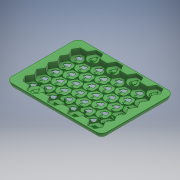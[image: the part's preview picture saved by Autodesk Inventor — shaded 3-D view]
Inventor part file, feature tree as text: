
AUTODESK INVENTOR PART (.ipt)
format: ipt  version: 2018 (Build 220112000, 112)  size: 8,218,624 bytes
history: native  units: mm
features: projected_geometry x23, extrude x22, sketch x19, pattern_linear x5, mirror x2, sweep x1, plane x1
ambient origin geometry x8: Origin, YZ Plane, XZ Plane, XY Plane, X Axis, Y Axis, Z Axis, Center Point
bodies: Solid1 (feature_tree)
feature tree (73):
  sketch  "Sketch1"  dims[d0=191.364mm d1=265.006mm]
  extrude  "Extrusion1"  Depth=265.006mm
  sketch  "Sketch2"  dims[d2=35.5mm d21=227.899911mm]
  extrude  "Extrusion3"  Depth=35.5mm
  sweep  "Sweep3"
  sketch  "Sketch6"  dims[d24=50.0mm d26=36.5mm d27=10.0mm d29=10.0mm]
  extrude  "Extrusion4"  Depth=10.0mm
  extrude  "Extrusion6"  Depth=10.0mm
  sketch  "Sketch7"  dims[d31=20.0mm d33=36.5mm d34=10.0mm d36=10.0mm]
  extrude  "Extrusion5"  Depth=10.0mm
  pattern_linear  "Rectangular Pattern1"  Count1=2 Spacing1=36.5mm
  extrude  "Extrusion7"  Depth=10.0mm
  extrude  "Extrusion8"  Depth=1.0mm
  extrude  "Extrusion9"  TaperAngle=0.0deg  [1 undecoded]
  sketch  "Sketch14"  dims[d45=16.65mm d46=0.0mm]
  extrude  "Extrusion12"  Depth=10.0mm TaperAngle=0.0deg
  extrude  "Extrusion13"  Depth=40.0mm
  extrude  "Extrusion15"  Depth=5.0mm TaperAngle=0.0deg
  extrude  "Extrusion16"  Depth=182.5mm
  extrude  "Extrusion17"  Depth=5.0mm TaperAngle=0.0deg
  extrude  "Extrusion27"  Depth=1.0mm TaperAngle=0.0deg
  extrude  "Extrusion18"  Depth=36.5mm
  extrude  "Extrusion19"  Depth=10.0mm
  extrude  "Extrusion20"  Depth=5.0mm TaperAngle=0.0deg
  plane  "Work Plane1"
  mirror  "Mirror1"
  pattern_linear  "Rectangular Pattern3"  Spacing1=0.5mm  [1 undecoded]
  pattern_linear  "Rectangular Pattern4"  Spacing1=11.65mm  [1 undecoded]
  extrude  "Extrusion21"  TaperAngle=0.0deg  [1 undecoded]
  extrude  "Extrusion22"  Depth=16.0mm
  extrude  "Extrusion23"  Depth=10.0mm
  pattern_linear  "Rectangular Pattern5"  Count1=8 Spacing1=31.609927mm
  pattern_linear  "Rectangular Pattern6"  Spacing1=11.65mm  [1 undecoded]
  mirror  "Mirror2"
  extrude  "Extrusion24"  TaperAngle=0.0deg  [1 undecoded]
  extrude  "Extrusion28"  Depth=16.0mm
  projected_geometry  "Projected Loop1"
  sketch  "Sketch5"  dims[d22=301.559911mm d23=18.288mm]
  projected_geometry  "Projected Loop3"
  projected_geometry  "Projected Loop4"
  sketch  "Sketch11"  dims[d38=40.0mm d40=63.219854mm d41=10.0mm d43=10.0mm]
  projected_geometry  "Projected Loop10"
  projected_geometry  "Projected Loop11"
  projected_geometry  "Projected Loop18"
  projected_geometry  "Projected Loop19"
  projected_geometry  "Projected Loop20"
  sketch  "Sketch16"  dims[d47=1.0mm d48=0.0mm]
  projected_geometry  "Projected Loop24"
  projected_geometry  "Projected Loop25"
  projected_geometry  "Projected Loop26"
  sketch  "Sketch17"  dims[d53=36.5mm d58=20.0mm d60=36.5mm]
  projected_geometry  "Projected Loop27"
  projected_geometry  "Projected Loop28"
  sketch  "Sketch18"  dims[d61=10.0mm d63=10.0mm d67=63.219854mm]
  projected_geometry  "Projected Loop29"
  sketch  "Sketch19"  dims[d72=1.0mm d73=0.0mm d80=0.2mm]
  projected_geometry  "Projected Loop30"
  projected_geometry  "Projected Loop31"
  sketch  "Sketch20"  dims[d81=18.288mm d82=0.0mm d83=0.0mm]
  projected_geometry  "Projected Loop32"
  sketch  "Sketch21"  dims[d84=10.0mm d85=0.0mm d86=0.5mm d87=0.0mm]
  projected_geometry  "Projected Loop33"
  sketch  "Sketch22"  dims[d88=40.0mm d90=63.219854mm d91=40.0mm d93=63.219854mm]
  projected_geometry  "Projected Loop34"
  sketch  "Sketch23"  dims[d94=10.0mm d96=10.0mm d98=5.0mm d99=0.0mm]
  projected_geometry  "Projected Loop35"
  sketch  "Sketch24"  dims[d100=20.0mm d102=182.5mm d103=10.0mm d105=10.0mm d107=182.5mm]
  projected_geometry  "Projected Loop36"
  sketch  "Sketch25"  dims[d108=5.0mm d109=0.0mm d110=4.5mm d111=0.0mm]
  sketch  "Sketch29"  dims[d112=10.0mm d113=0.0mm d134=1.0mm d135=0.0mm]
  projected_geometry  "Projected Loop39"
  sketch  "Sketch30"  dims[d136=0.5mm d137=0.0mm d146=20.0mm d148=36.5mm d149=10.0mm d151=10.0mm d167=0.5mm d168=0.0mm d169=0.5mm d170=0.0mm d171=11.65mm d172=0.0mm d180=16.0mm d181=10.0mm d182=80.0mm d184=31.609927mm d185=10.0mm d187=10.0mm d189=11.65mm d190=0.0mm d191=16.0mm d192=10.0mm d193=11.65mm d194=0.0mm d195=10.0mm d196=16.0mm d197=11.65mm d198=0.0mm d205=40.0mm d207=36.5mm d208=30.0mm d210=63.219854mm d211=40.0mm d213=36.5mm d214=20.0mm d216=189.659563mm d217=16.0mm d218=8.0mm d219=11.65mm d220=0.0mm d221=16.0mm d222=8.0mm d223=11.65mm d224=0.0mm d225=8.0mm d226=16.0mm d227=11.65mm d228=0.0mm d229=40.0mm d231=63.219854mm d232=30.0mm d234=63.219854mm d235=11.65mm d236=0.0mm d250=0.85mm d251=0.0mm d252=15.0mm d254=5.0mm d255=0.0mm d256=9.0mm]
  projected_geometry  "Projected Loop40"
note: 6 required parameter values undecoded (feature->parameter linkage not recoverable at this tier; creation-order binding heuristic only, values carry confidence <= 0.55)
